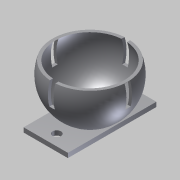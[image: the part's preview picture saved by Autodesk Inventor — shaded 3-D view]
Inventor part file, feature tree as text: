
AUTODESK INVENTOR PART (.ipt)
format: ipt  version: 2012 SP2 (Build 160219200, 219)  size: 237,568 bytes
history: native  units: in
note: dims shown in document units (in); Inventor stores cm internally (conversion verified against a paired STEP export)
features: sketch x10, extrude x9, plane x4, revolve x1, loft x1
ambient origin geometry x8: Origin, YZ Plane, XZ Plane, XY Plane, X Axis, Y Axis, Z Axis, Center Point
bodies: Solid1 (feature_tree)
feature tree (25):
  sketch  "Sketch1"  dims[d0=1.65in d1=0.065in]
  plane  "Work Plane1"
  sketch  "Sketch2"  dims[d8=0.125in d11=0.125in]
  plane  "Work Plane4"
  sketch  "Sketch5"  dims[d16=90.0deg d17=1.0in d18=0.0in]
  plane  "Work Plane5"
  sketch  "Sketch6"  dims[d19=1.0in d20=0.0in d21=1.75in]
  revolve  "Revolution2"  [1 undecoded]
  extrude  "Extrusion6"  Depth=0.125in
  extrude  "Extrusion7"  Depth=1.0in TaperAngle=0.0deg
  plane  "Work Plane6"
  loft  "Loft1"
  extrude  "Extrusion8"  TaperAngle=0.0deg  [1 undecoded]
  extrude  "Extrusion9"  Depth=0.275in
  extrude  "Extrusion10"  Depth=1.0in TaperAngle=0.0deg
  sketch  "Sketch11"  dims[d35=0.1875in d36=1.5in]
  extrude  "Extrusion14"  Depth=0.1875in
  extrude  "Extrusion15"  Depth=1.5in
  extrude  "Extrusion16"  Depth=1.0in TaperAngle=0.0deg
  extrude  "Extrusion17"  Depth=1.0in TaperAngle=0.0deg
  sketch  "Sketch7"  dims[d22=0.0in d23=90.0deg d24=0.0in d25=90.0deg]
  sketch  "Sketch8"  dims[d26=1.0in d27=0.0in d28=0.275in]
  sketch  "Sketch9"  dims[d29=0.065in d30=0.0in d31=1.0in d32=0.0in]
  sketch  "Sketch10"  dims[d33=2.0in d34=0.1875in]
  sketch  "Sketch14"  dims[d49=1.0in d50=1.0in d51=0.0in d52=1.0in d53=0.0in d54=1.0in d55=0.0in d56=1.0in d57=0.0in]
note: 2 required parameter values undecoded (feature->parameter linkage not recoverable at this tier; creation-order binding heuristic only, values carry confidence <= 0.55)